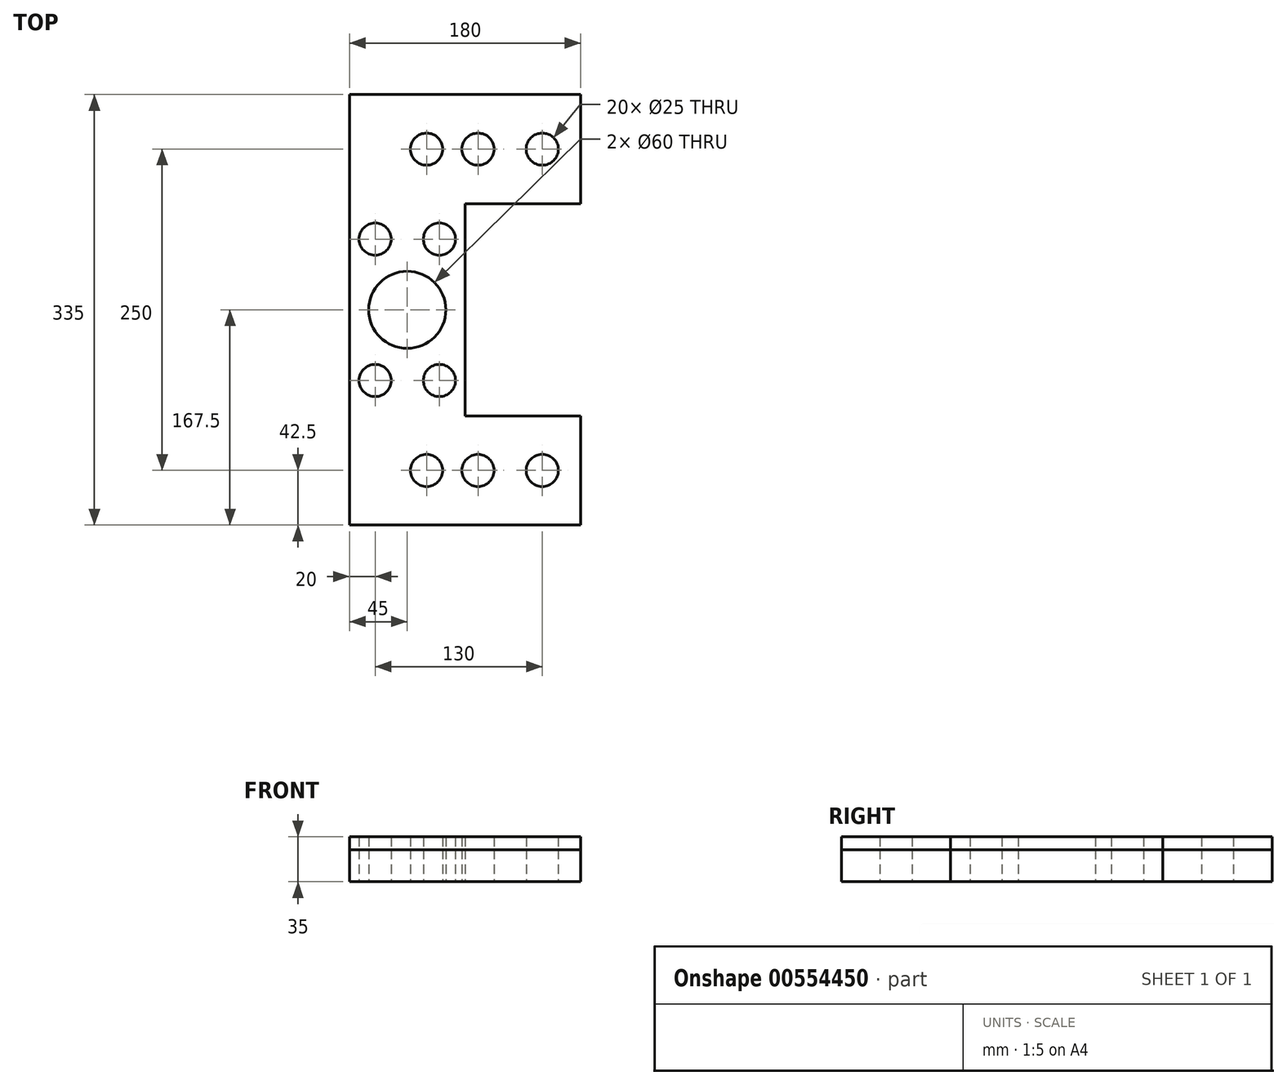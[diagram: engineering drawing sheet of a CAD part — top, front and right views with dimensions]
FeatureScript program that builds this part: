
annotation { "Feature Type Name" : "Feature", "Feature Type Description" : "" }
export const myFeature = defineFeature(function(context is Context, id is Id, definition is map)
    precondition{}
    {
        {
            var Q0;
            Q0=qCreatedBy(makeId("Top.planeOp"),FACE);
            var sketch = newSketch(context, id + "F0", { "sketchPlane" : qUnion([Q0])});
            skLineSegment(sketch, "E0", {"start": v(-25, 82.5) * mm, "end": v(65, 82.5) * mm});
            skLineSegment(sketch, "E1", {"start": v(65, 82.5) * mm, "end": v(65, 167.5) * mm});
            skLineSegment(sketch, "E2", {"start": v(65, 167.5) * mm, "end": v(-115, 167.5) * mm});
            skLineSegment(sketch, "E3", {"start": v(-115, 167.5) * mm, "end": v(-115, -167.5) * mm});
            skLineSegment(sketch, "E4", {"start": v(-115, -167.5) * mm, "end": v(65, -167.5) * mm});
            skLineSegment(sketch, "E5", {"start": v(65, -167.5) * mm, "end": v(65, -82.5) * mm});
            skLineSegment(sketch, "E6", {"start": v(65, -82.5) * mm, "end": v(-25, -82.5) * mm});
            skLineSegment(sketch, "E7", {"start": v(-25, 82.5) * mm, "end": v(-25, 0) * mm});
            skLineSegment(sketch, "E8", {"start": v(-25, 0) * mm, "end": v(-25, -82.5) * mm});
            skLineSegment(sketch, "E9", {"start": v(171.7, 82.5) * mm, "end": v(-167.86, 82.5) * mm, "construction": true});
            skLineSegment(sketch, "E10", {"start": v(171.7, -82.5) * mm, "end": v(-167.86, -82.5) * mm, "construction": true});
            skCircle(sketch, "E11", {"center": v(-95, 55) * mm, "radius": 12.5 * mm});
            skCircle(sketch, "E12", {"center": v(-45, 55) * mm, "radius": 12.5 * mm});
            skCircle(sketch, "E13", {"center": v(-95, -55) * mm, "radius": 12.5 * mm});
            skCircle(sketch, "E14", {"center": v(-45, -55) * mm, "radius": 12.5 * mm});
            skCircle(sketch, "E15", {"center": v(-70, 0) * mm, "radius": 30 * mm});
            skLineSegment(sketch, "E16", {"start": v(-165.93, 125) * mm, "end": v(147.35, 125) * mm, "construction": true});
            skLineSegment(sketch, "E17", {"start": v(-167.86, -125) * mm, "end": v(147.35, -125) * mm, "construction": true});
            skCircle(sketch, "E18", {"center": v(-55, 125) * mm, "radius": 12.5 * mm});
            skCircle(sketch, "E19", {"center": v(-15, 125) * mm, "radius": 12.5 * mm});
            skCircle(sketch, "E20", {"center": v(35, 125) * mm, "radius": 12.5 * mm});
            skCircle(sketch, "E21", {"center": v(-55, -125) * mm, "radius": 12.5 * mm});
            skCircle(sketch, "E22", {"center": v(-15, -125) * mm, "radius": 12.5 * mm});
            skCircle(sketch, "E23", {"center": v(35, -125) * mm, "radius": 12.5 * mm});
            skSolve(sketch);
        }
        {
            var Q0;
            Q0=makeQuery(id+"F0.imprint","IMPRINT",FACE,{"disambiguationData":[TD([[makeQuery(id+"F0.imprint","IMPRINT",EDGE,{"derivedFrom":sQuery(id+"F0.wireOp",EDGE,"E0")}),1.0]])]});
            extrude(context, id + "F1", {"entities" : qUnion([Q0]), "depth" : 25 * mm, "offsetDistance" : 25 * mm});
        }
        {
            var Q0;
            Q0=makeQuery(id+"F1.opExtrude","CAP_FACE",FACE,{"disambiguationData":[OSD([sQuery(id+"F0.wireOp",EDGE,"E0"),sQuery(id+"F0.wireOp",EDGE,"E1"),sQuery(id+"F0.wireOp",EDGE,"E2"),sQuery(id+"F0.wireOp",EDGE,"E3"),sQuery(id+"F0.wireOp",EDGE,"E4"),sQuery(id+"F0.wireOp",EDGE,"E5"),sQuery(id+"F0.wireOp",EDGE,"E6"),sQuery(id+"F0.wireOp",EDGE,"E7"),sQuery(id+"F0.wireOp",EDGE,"E8"),sQuery(id+"F0.wireOp",EDGE,"E11"),sQuery(id+"F0.wireOp",EDGE,"E12"),sQuery(id+"F0.wireOp",EDGE,"E13"),sQuery(id+"F0.wireOp",EDGE,"E14"),sQuery(id+"F0.wireOp",EDGE,"E15"),sQuery(id+"F0.wireOp",EDGE,"E18"),sQuery(id+"F0.wireOp",EDGE,"E19"),sQuery(id+"F0.wireOp",EDGE,"E20"),sQuery(id+"F0.wireOp",EDGE,"E21"),sQuery(id+"F0.wireOp",EDGE,"E22"),sQuery(id+"F0.wireOp",EDGE,"E23")])],"isStart":false});
            extrude(context, id + "F2", {"entities" : qUnion([Q0]), "depth" : 10 * mm, "offsetDistance" : 25 * mm});
        }
    });
